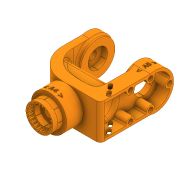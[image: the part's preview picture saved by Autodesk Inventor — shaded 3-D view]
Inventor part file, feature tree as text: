
AUTODESK INVENTOR PART (.ipt)
format: ipt  version: 2020 (Build 240168000, 168)  size: 2,008,576 bytes
history: native  units: in
note: dims shown in document units (in); Inventor stores cm internally (conversion verified against a paired STEP export)
features: sketch x41, extrude x37, projected_geometry x29, chamfer x6, plane x6, fillet x6, emboss x3
ambient origin geometry x8: Origin, YZ Plane, XZ Plane, XY Plane, X Axis, Y Axis, Z Axis, Center Point
bodies: Solid1 (feature_tree)
feature tree (128):
  extrude  "Extrusion1"  Depth=2.0472in
  extrude  "Extrusion2"  Depth=1.1063in
  chamfer  "Chamfer2"  Distance=0.2756in
  extrude  "Extrusion4"  Depth=0.0157in
  extrude  "Extrusion7"  Depth=0.2756in TaperAngle=0.0deg
  chamfer  "Chamfer4"  Distance=0.0394in
  extrude  "Extrusion8"  Depth=0.0157in
  sketch  "Sketch12"  dims[d39=1.4567in d57=0.0394in d58=0.0in]
  plane  "Work Plane1"
  sketch  "Sketch13"  dims[d59=0.315in d60=0.125in d61=0.0137in d67=0.0157in]
  extrude  "Extrusion10"  Depth=0.0394in TaperAngle=0.0deg
  extrude  "Extrusion11"  Depth=0.0866in
  chamfer  "Chamfer5"  Distance=9.4488in Angle=360.0deg
  extrude  "Extrusion12"  Depth=0.2756in TaperAngle=0.0deg
  plane  "Work Plane2"
  extrude  "Extrusion13"  Depth=0.315in
  plane  "Work Plane3"
  extrude  "Extrusion14"  Depth=1.0236in
  extrude  "Extrusion15"  Depth=0.8858in
  extrude  "Extrusion16"  Depth=0.3937in
  extrude  "Extrusion17"  Depth=1.378in
  sketch  "Sketch21"  dims[d107=0.315in d108=0.0in d109=0.315in d110=0.125in d111=0.0137in]
  extrude  "Extrusion19"  Depth=0.5906in
  sketch  "Sketch23"  dims[d112=1.0in d113=0.0in d114=1.0236in]
  extrude  "Extrusion20"  Depth=0.1575in TaperAngle=0.0deg
  extrude  "Extrusion21"  Depth=0.1575in TaperAngle=0.0deg
  extrude  "Extrusion22"  Depth=4.2323in
  extrude  "Extrusion23"  Depth=0.1575in
  extrude  "Extrusion24"  Depth=1.1024in
  extrude  "Extrusion25"  Depth=0.4921in
  extrude  "Extrusion26"  Depth=0.75in
  extrude  "Extrusion27"  Depth=0.2165in TaperAngle=0.0deg
  extrude  "Extrusion28"  Depth=0.1575in
  extrude  "Extrusion29"  Depth=1.1811in
  plane  "Work Plane4"
  extrude  "Extrusion30"  Depth=0.3937in TaperAngle=0.0deg
  fillet  "Fillet1"  Radius=0.3937in
  fillet  "Fillet2"  Radius=0.315in
  extrude  "Extrusion31"  Depth=0.315in TaperAngle=0.0deg
  extrude  "Extrusion32"  Depth=0.315in TaperAngle=0.0deg
  extrude  "Extrusion33"  Depth=0.3937in TaperAngle=0.0deg
  fillet  "Fillet3"  Radius=0.2165in
  extrude  "Extrusion34"  Depth=0.4724in
  chamfer  "Chamfer6"  Distance=0.2756in
  chamfer  "Chamfer7"  Distance=0.0394in
  extrude  "Extrusion35"  Depth=0.001in
  extrude  "Extrusion36"  Depth=1.0in TaperAngle=0.0deg
  fillet  "Fillet5"  Radius=0.1575in
  extrude  "Extrusion38"  Depth=0.315in
  extrude  "Extrusion39"  Depth=0.122in
  extrude  "Extrusion40"  Depth=0.122in TaperAngle=360.0deg
  fillet  "Fillet7"  Radius=1.0in
  extrude  "Extrusion41"  Depth=0.122in TaperAngle=0.0deg
  chamfer  "Chamfer8"  Distance=0.1969in
  extrude  "Extrusion42"  Depth=0.122in TaperAngle=0.0deg
  plane  "Work Plane6"
  emboss  "Emboss1"
  emboss  "Emboss2"
  plane  "Work Plane7"
  emboss  "Emboss3"
  extrude  "Extrusion43"  Depth=0.122in
  fillet  "Fillet9"  Radius=0.0787in
  sketch  "Sketch1"  dims[d0=0.6299in d1=2.0472in]
  sketch  "Sketch2"  dims[d2=0.9449in d3=0.0in d4=1.1063in]
  sketch  "Sketch4"  dims[d5=1.5748in d6=0.2756in d7=0.0in]
  sketch  "Sketch8"  dims[d11=0.2756in d12=0.125in d13=0.0137in d25=0.0157in]
  projected_geometry  "Projected Loop2"
  sketch  "Sketch10"  dims[d26=6.2992in d28=360.0deg d30=0.2756in d31=0.0in]
  sketch  "Sketch14"  dims[d68=4.7244in d70=360.0deg d72=0.0394in d73=0.0in]
  sketch  "Sketch15"  dims[d83=0.0591in d84=0.0866in]
  projected_geometry  "Projected Loop4"
  sketch  "Sketch16"  dims[d85=0.0827in]
  sketch  "Sketch17"  dims[d86=0.0827in]
  projected_geometry  "Projected Loop5"
  sketch  "Sketch18"  dims[d87=0.0827in d88=9.4488in d90=360.0deg]
  projected_geometry  "Projected Loop6"
  projected_geometry  "Projected Loop7"
  sketch  "Sketch19"  dims[d92=0.2756in]
  projected_geometry  "Projected Loop8"
  projected_geometry  "Projected Loop9"
  sketch  "Sketch20"  dims[d94=9.4488in d95=0.0827in d96=0.0827in d97=0.0827in d98=360.0deg d105=0.2756in d106=0.0in]
  projected_geometry  "Projected Loop10"
  projected_geometry  "Projected Loop11"
  projected_geometry  "Projected Loop12"
  projected_geometry  "Projected Loop13"
  sketch  "Sketch25"  dims[d115=0.7874in d117=0.8858in]
  sketch  "Sketch26"  dims[d118=2.7559in d119=0.3937in]
  projected_geometry  "Projected Loop16"
  projected_geometry  "Projected Loop17"
  sketch  "Sketch27"  dims[d120=0.5906in d121=1.378in]
  projected_geometry  "Projected Loop18"
  projected_geometry  "Projected Loop19"
  sketch  "Sketch28"  dims[d123=3.4941in d124=0.5906in]
  projected_geometry  "Projected Loop20"
  projected_geometry  "Projected Loop21"
  sketch  "Sketch29"  dims[d126=1.9685in d129=0.1575in d130=0.0in]
  projected_geometry  "Projected Loop22"
  projected_geometry  "Projected Loop23"
  sketch  "Sketch30"  dims[d131=-2.0472in d132=0.1575in d133=0.0in]
  projected_geometry  "Projected Loop24"
  sketch  "Sketch31"  dims[d134=2.126in d136=4.2323in]
  sketch  "Sketch32"  dims[d137=0.1575in d138=0.1575in]
  sketch  "Sketch34"  dims[d139=0.4921in d140=0.0in d141=1.1024in]
  projected_geometry  "Projected Loop25"
  sketch  "Sketch35"  dims[d142=1.1614in d143=0.4921in]
  sketch  "Sketch36"  dims[d144=0.3445in d145=0.75in]
  projected_geometry  "Projected Loop26"
  sketch  "Sketch37"  dims[d146=0.1575in d147=0.0in d148=0.2165in d149=0.0in]
  projected_geometry  "Projected Loop27"
  sketch  "Sketch38"  dims[d152=1.0039in d153=0.0in d154=0.1575in]
  projected_geometry  "Projected Loop28"
  sketch  "Sketch39"  dims[d155=0.1575in d160=1.1811in]
  projected_geometry  "Projected Loop29"
  sketch  "Sketch40"  dims[d161=0.1969in d162=0.0in d163=0.315in d164=0.0in d165=0.3937in d166=0.0in d167=0.315in d168=0.0in]
  sketch  "Sketch41"  dims[d169=0.315in d170=0.0in d171=0.315in d172=0.0in]
  projected_geometry  "Projected Loop30"
  sketch  "Sketch43"  dims[d173=0.315in d174=0.0in d175=0.315in d176=0.0in]
  projected_geometry  "Projected Loop31"
  sketch  "Sketch44"  dims[d177=1.1024in d178=0.3937in d179=0.0in d180=0.2165in d181=0.0in]
  sketch  "Sketch45"  dims[d183=-0.0197in d184=0.4724in d185=0.2756in d186=0.0in]
  sketch  "Sketch46"  dims[d187=0.5512in]
  projected_geometry  "Projected Loop32"
  sketch  "Sketch47"  dims[d188=0.2165in d189=0.0394in d190=0.0in]
  projected_geometry  "Projected Loop33"
  sketch  "Sketch48"  dims[d191=0.0394in d192=0.0in d193=0.001in]
  sketch  "Sketch49"  dims[d194=0.001in d195=1.0in d196=0.0in d197=0.1575in]
  sketch  "Sketch50"  dims[d198=1.0in d199=0.0in d200=0.315in d201=0.125in d202=0.0137in]
  sketch  "Sketch52"  dims[d203=0.315in d204=0.125in d205=0.0137in d206=0.0157in d207=2.3622in d209=360.0deg d211=1.0in d212=0.0in d213=1.0in d214=0.0in d221=0.1969in d222=0.1969in d223=0.0in d224=0.1575in d225=0.0787in d226=0.1969in d227=0.0in d229=0.1181in d230=1.0039in d231=0.4134in d232=0.5118in d233=0.0984in d235=0.0197in d236=0.1181in d237=0.1181in d238=0.1969in d239=0.1969in d240=0.0in d241=0.0in d242=0.2362in d243=0.0787in d244=0.0787in d251=0.0787in d252=0.0787in d253=0.2756in d254=0.4724in d255=0.2756in d256=0.4724in d257=0.2756in d258=0.4724in d259=0.2756in d260=0.4724in d261=0.1575in d262=0.0in d263=0.0787in d264=0.125in d265=45.0deg d266=1.0in d267=0.0in d269=0.0394in d270=0.0in d271=0.0394in d272=0.0in d273=0.0394in d274=0.0in d275=0.0039in d276=0.0787in d277=1.0in d278=0.0in d279=0.122in]
